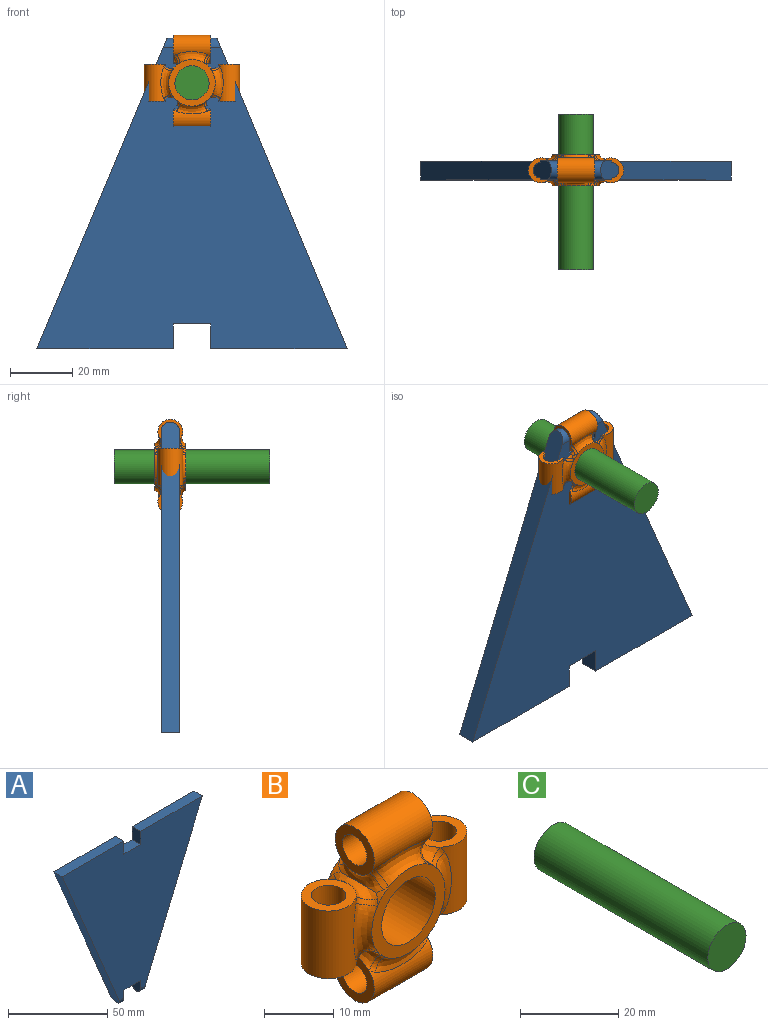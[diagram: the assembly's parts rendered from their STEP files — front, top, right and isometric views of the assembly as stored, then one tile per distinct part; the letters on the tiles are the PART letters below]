
ASSEMBLY  parts=3 mates=2
PART A: 16 faces, bbox 100x6x100 mm
  f0: plane 100x42mm, normal (-0.92,0,-0.39), area 646.6mm2, adj f4,f5,f8,f13,f15
  f1: plane 8x6mm, normal (1,0,0), area 44.1mm2, adj f4,f5,f9,f13,f15
  f2: plane 8x6mm, normal (-1,0,0), area 44.1mm2, adj f4,f5,f9,f12,f14
  f3: plane 100x42mm, normal (0.92,0,-0.39), area 646.6mm2, adj f4,f5,f10,f12,f14
  f4: plane 100x96.96mm, normal (0,-1,0), area 5592mm2, adj f0,f1,f2,f3,f6,f7,f8,f9
  f5: plane 100x97mm, normal (0,1,0), area 5592.2mm2, adj f0,f1,f2,f3,f6,f7,f8,f9
  f6: plane 12x6mm, normal (0,0,1), area 72mm2, adj f4,f5,f7,f11
  f7: plane 8x6mm, normal (1,0,0), area 48mm2, adj f4,f5,f6,f8
  f8: plane 44x6mm, normal (0,0,1), area 264mm2, adj f0,f4,f5,f7
  f9: plane 12x6mm, normal (0,0,-1), area 72mm2, adj f1,f2,f4,f5
  f10: plane 44x6mm, normal (0,0,1), area 264mm2, adj f3,f4,f5,f11
  f11: plane 8x6mm, normal (-1,0,0), area 48mm2, adj f4,f5,f6,f10
  f12: cylinder r=3mm len=6mm, axis (1,0,0), area 23.4mm2, adj f2,f3,f5,f14
  f13: cylinder r=3mm len=6mm, axis (1,0,0), area 23.4mm2, adj f0,f1,f5,f15
  f14: plane 3.29x0.04mm, normal (0,1,-0.03), area 0.1mm2, adj f2,f3,f4,f12
  f15: plane 3.29x0.04mm, normal (0,1,-0.03), area 0.1mm2, adj f0,f1,f4,f13
PART B: 59 faces, bbox 31x11x31 mm
  f0: cylinder r=7.5mm len=2.31mm, axis (0,1,0), area 1.9mm2, adj f6,f13,f23,f39,f41
  f1: cylinder r=7.5mm len=2.31mm, axis (0,1,0), area 1.9mm2, adj f9,f13,f31,f42,f44
  f2: cylinder r=7.5mm len=2.31mm, axis (0,1,0), area 1.9mm2, adj f6,f14,f24,f39,f40
  f3: cylinder r=7.5mm len=2.31mm, axis (0,1,0), area 1.9mm2, adj f7,f13,f27,f51,f52
  f4: cylinder r=7.5mm len=2.31mm, axis (0,1,0), area 1.9mm2, adj f7,f14,f28,f51,f53
  f5: cylinder r=7.5mm len=2.31mm, axis (0,1,0), area 1.9mm2, adj f8,f14,f32,f57,f58
  f6: bspline ~9.2x4.13mm, area 19.4mm2, adj f0,f2,f22,f23,f24,f39
  f7: bspline ~9.2x4.13mm, area 19.4mm2, adj f3,f4,f21,f27,f28,f51
  f8: bspline ~9.2x4.12mm, area 19.4mm2, adj f5,f11,f17,f30,f32,f58
  f9: bspline ~9.2x4.12mm, area 19.4mm2, adj f1,f10,f18,f31,f33,f42
  f10: cylinder r=7.5mm len=2.31mm, axis (0,1,0), area 1.9mm2, adj f9,f14,f33,f42,f43
  f11: cylinder r=7.5mm len=2.31mm, axis (0,1,0), area 1.9mm2, adj f8,f13,f30,f56,f58
  f12: cylinder r=5.5mm len=11mm, axis (0,1,0), area 345.6mm2, adj f13,f14
  f13: plane 15.06x15.06mm, normal (0,-1,0), area 81.7mm2, adj f0,f1,f3,f11,f12,f25,f29,f46
  f14: plane 15.06x15.06mm, normal (0,1,0), area 81.7mm2, adj f2,f4,f5,f10,f12,f26,f34,f45
  f15: cylinder r=4mm len=12mm, axis (0,0,1), area 193.7mm2, adj f17,f18,f29,f30,f31,f32,f33,f34
  f16: cylinder r=2.5mm len=12mm, axis (0,0,1), area 188.5mm2, adj f17,f18
  f17: plane 8.3x8.3mm, normal (0,0,-1), area 30.6mm2, adj f8,f15,f16
  f18: plane 8.3x8.3mm, normal (0,0,1), area 30.6mm2, adj f9,f15,f16
  f19: cylinder r=4mm len=12mm, axis (0,0,1), area 193.7mm2, adj f21,f22,f23,f24,f25,f26,f27,f28
  f20: cylinder r=2.5mm len=12mm, axis (0,0,1), area 188.5mm2, adj f21,f22
  f21: plane 8.3x8.3mm, normal (0,0,-1), area 30.6mm2, adj f7,f19,f20
  f22: plane 8.3x8.3mm, normal (0,0,1), area 30.6mm2, adj f6,f19,f20
  f23: bspline ~4.05x3.87mm, area 3.7mm2, adj f0,f6,f19,f25
  f24: bspline ~4.12x3.97mm, area 3.7mm2, adj f2,f6,f19,f26
  f25: bspline ~10.64x3.82mm, area 30.3mm2, adj f13,f19,f23,f27
  f26: bspline ~10.64x3.82mm, area 30.3mm2, adj f14,f19,f24,f28
  f27: bspline ~3.85x3.63mm, area 3.7mm2, adj f3,f7,f19,f25
  f28: bspline ~3.84x3.63mm, area 3.7mm2, adj f4,f7,f19,f26
  f29: bspline ~10.64x3.83mm, area 30.3mm2, adj f13,f15,f30,f31
  f30: bspline ~3.92x3.71mm, area 3.7mm2, adj f8,f11,f15,f29
  f31: bspline ~4.2x4.05mm, area 3.7mm2, adj f1,f9,f15,f29
  f32: bspline ~3.85x3.63mm, area 3.7mm2, adj f5,f8,f15,f34
  f33: bspline ~4.05x3.87mm, area 3.7mm2, adj f9,f10,f15,f34
  f34: bspline ~10.64x3.83mm, area 30.3mm2, adj f14,f15,f32,f33
  f35: cylinder r=2.5mm len=12mm, axis (1,0,0), area 188.5mm2, adj f37,f38
  f36: cylinder r=4mm len=12mm, axis (1,0,0), area 193.7mm2, adj f37,f38,f40,f41,f43,f44,f45,f46
  f37: plane 8.3x8.3mm, normal (1,0,0), area 30.6mm2, adj f35,f36,f39
  f38: plane 8.3x8.3mm, normal (-1,0,0), area 30.6mm2, adj f35,f36,f42
  f39: bspline ~9.2x4.12mm, area 19.4mm2, adj f0,f2,f6,f37,f40,f41
  f40: bspline ~4.05x3.87mm, area 3.7mm2, adj f2,f36,f39,f45
  f41: bspline ~4.2x4.05mm, area 3.7mm2, adj f0,f36,f39,f46
  f42: bspline ~9.2x4.12mm, area 19.4mm2, adj f1,f9,f10,f38,f43,f44
  f43: bspline ~3.85x3.63mm, area 3.7mm2, adj f10,f36,f42,f45
  f44: bspline ~3.92x3.71mm, area 3.7mm2, adj f1,f36,f42,f46
  f45: bspline ~10.64x3.83mm, area 30.3mm2, adj f14,f36,f40,f43
  f46: bspline ~10.64x3.83mm, area 30.3mm2, adj f13,f36,f41,f44
  f47: cylinder r=4mm len=12mm, axis (1,0,0), area 193.7mm2, adj f49,f50,f52,f53,f54,f55,f56,f57
  f48: cylinder r=2.5mm len=12mm, axis (1,0,0), area 188.5mm2, adj f49,f50
  f49: plane 8.3x8.3mm, normal (-1,0,0), area 30.6mm2, adj f47,f48,f58
  f50: plane 8.3x8.3mm, normal (1,0,0), area 30.6mm2, adj f47,f48,f51
  f51: bspline ~9.2x4.13mm, area 19.4mm2, adj f3,f4,f7,f50,f52,f53
  f52: bspline ~4.05x3.87mm, area 3.7mm2, adj f3,f47,f51,f54
  f53: bspline ~4.12x3.97mm, area 3.7mm2, adj f4,f47,f51,f55
  f54: bspline ~10.64x3.82mm, area 30.3mm2, adj f13,f47,f52,f56
  f55: bspline ~10.64x3.82mm, area 30.3mm2, adj f14,f47,f53,f57
  f56: bspline ~3.85x3.63mm, area 3.7mm2, adj f11,f47,f54,f58
  f57: bspline ~3.84x3.63mm, area 3.7mm2, adj f5,f47,f55,f58
  f58: bspline ~9.2x4.13mm, area 19.4mm2, adj f5,f8,f11,f49,f56,f57
PART C: 3 faces, bbox 11x50x11 mm
  f0: cylinder r=5.5mm len=50mm, axis (0,1,0), area 1727.9mm2, adj f1,f2
  f1: plane 11x11mm, normal (0,-1,0), area 95mm2, adj f0
  f2: plane 11x11mm, normal (0,1,0), area 95mm2, adj f0
PLACE A rot(axis=(0,1,0),180deg) t=(-18.06,-4.44,11.31)mm
PLACE B t=(-18.06,-2.44,-3.02)mm
PLACE C t=(-18.06,10.58,-3.02)mm
MATE fastened A.f12 <-> B.f35  axis (-1,0,0) through (-12.06,-7.44,8.31)mm
MATE slider B.f12 <-> C.f0  axis (0,1,0) through (-18.06,-12.44,-3.02)mm
